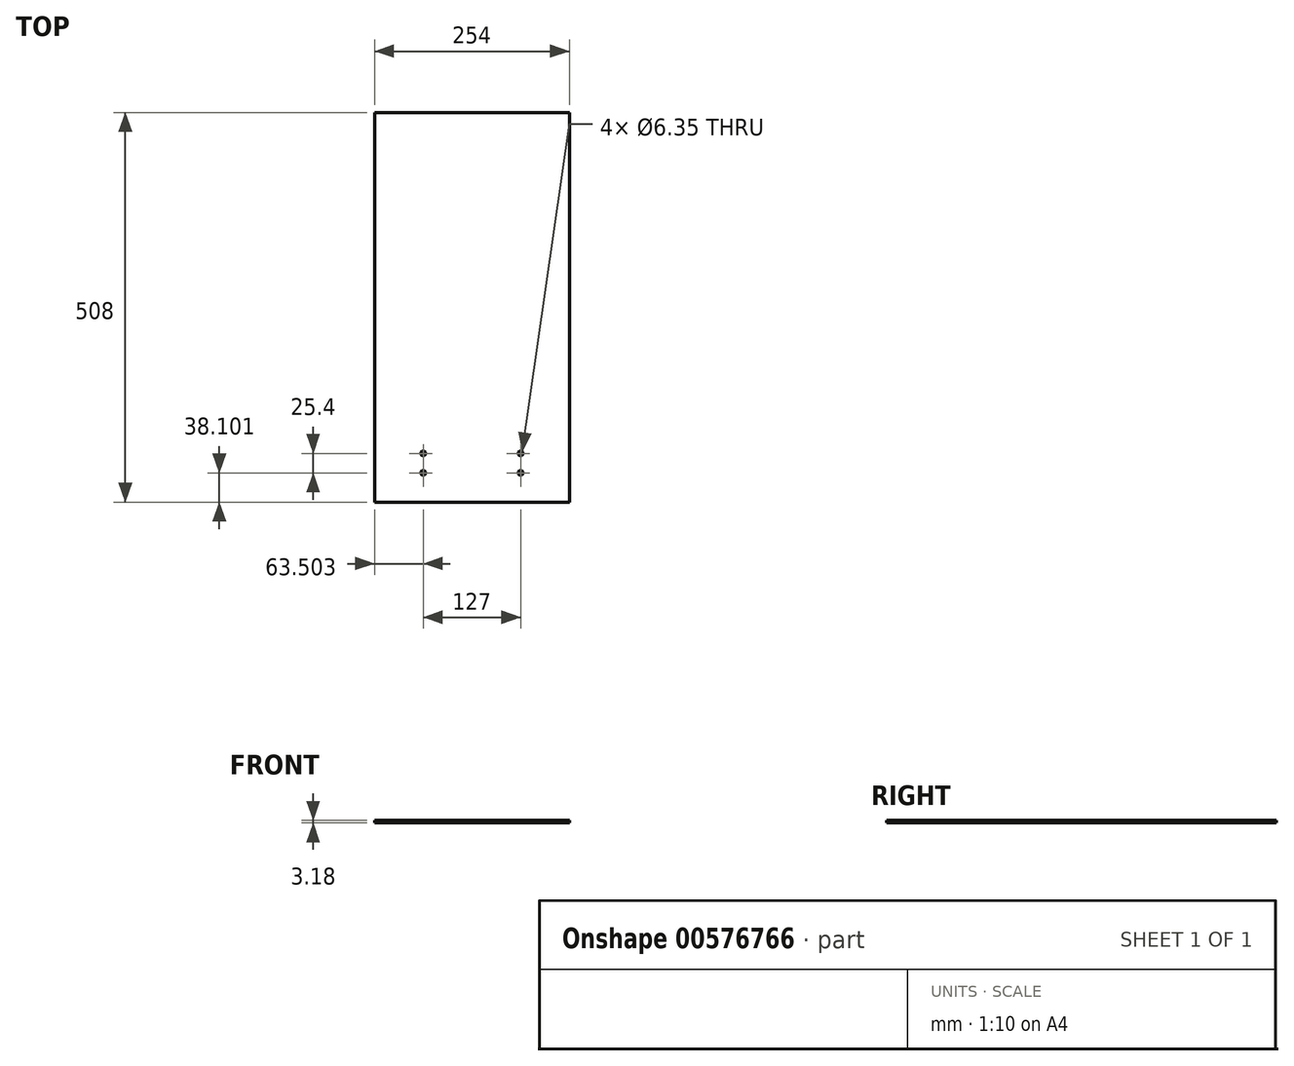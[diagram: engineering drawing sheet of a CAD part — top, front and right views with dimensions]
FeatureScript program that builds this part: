
annotation { "Feature Type Name" : "Feature", "Feature Type Description" : "" }
export const myFeature = defineFeature(function(context is Context, id is Id, definition is map)
    precondition{}
    {
        {
            var Q0;
            Q0=qCreatedBy(makeId("Top.planeOp"),FACE);
            var sketch = newSketch(context, id + "F0", { "sketchPlane" : qUnion([Q0])});
            skLineSegment(sketch, "E0.bottom", {"start": v(-112.49, 399) * mm, "end": v(141.51, 399) * mm});
            skLineSegment(sketch, "E0.top", {"start": v(-112.49, -109) * mm, "end": v(141.51, -109) * mm});
            skLineSegment(sketch, "E0.left", {"start": v(-112.49, 399) * mm, "end": v(-112.49, -109) * mm});
            skLineSegment(sketch, "E0.right", {"start": v(141.51, 399) * mm, "end": v(141.51, -109) * mm});
            skSolve(sketch);
        }
        {
            var Q0;
            Q0 = qSketchRegion(id + "F0", true);
            extrude(context, id + "F1", {"entities" : qUnion([Q0]), "depth" : 3.17 * mm, "offsetDistance" : 25.4 * mm});
        }
        {
            var Q0;
            Q0=makeQuery(id+"F1.opExtrude","CAP_FACE",FACE,{"disambiguationData":[OSD([sQuery(id+"F0.wireOp",EDGE,"E0.bottom"),sQuery(id+"F0.wireOp",EDGE,"E0.top"),sQuery(id+"F0.wireOp",EDGE,"E0.left"),sQuery(id+"F0.wireOp",EDGE,"E0.right")])],"isStart":false});
            var sketch = newSketch(context, id + "F2", { "sketchPlane" : qUnion([Q0])});
            skCircle(sketch, "E1", {"center": v(-48.99, -45.5) * mm, "radius": 3.18 * mm});
            skCircle(sketch, "E2", {"center": v(78.01, -45.5) * mm, "radius": 3.18 * mm});
            skCircle(sketch, "E3", {"center": v(-48.99, -70.9) * mm, "radius": 3.18 * mm});
            skCircle(sketch, "E4", {"center": v(78.01, -70.9) * mm, "radius": 3.18 * mm});
            skSolve(sketch);
        }
        {
            var Q0;
            Q0 = qSketchRegion(id + "F2", true);
            extrude(context, id + "F3", {"entities" : qUnion([Q0]), "operationType" : NewBodyOperationType.REMOVE, "endBound" : BoundingType.THROUGH_ALL, "oppositeDirection" : true, "depth" : 25.4 * mm, "offsetDistance" : 25.4 * mm});
        }
    });
